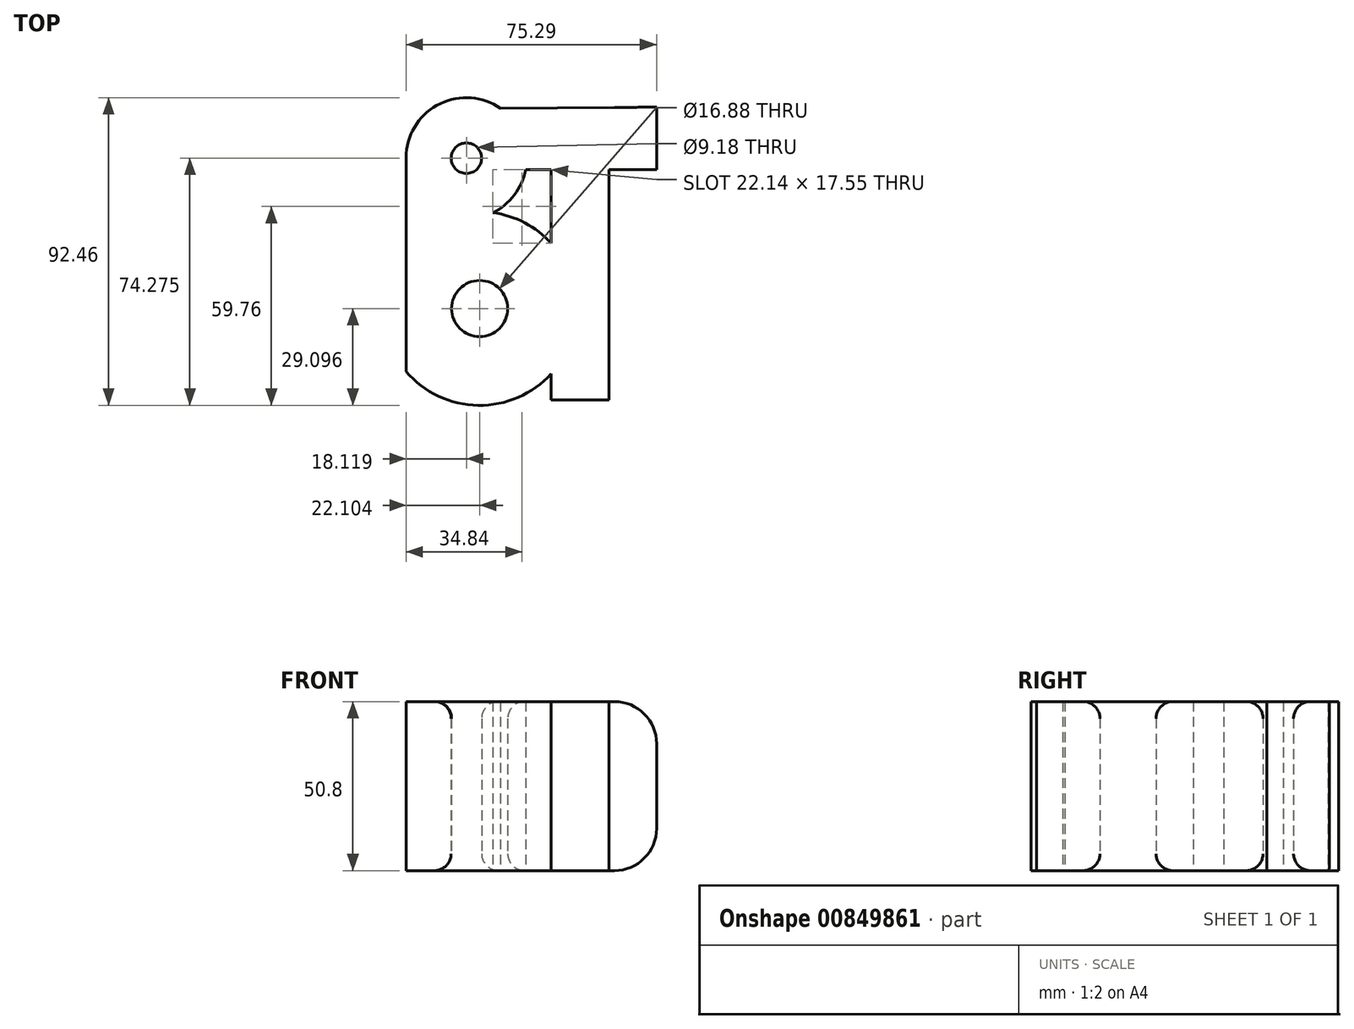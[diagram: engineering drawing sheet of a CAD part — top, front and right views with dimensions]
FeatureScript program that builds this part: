
annotation { "Feature Type Name" : "Feature", "Feature Type Description" : "" }
export const myFeature = defineFeature(function(context is Context, id is Id, definition is map)
    precondition{}
    {
        {
            var Q0;
            Q0=qCreatedBy(makeId("Top.planeOp"),FACE);
            var sketch = newSketch(context, id + "F0", { "sketchPlane" : qUnion([Q0])});
            skLineSegment(sketch, "E0", {"start": v(-40.97, 20.71) * mm, "end": v(-40.97, -44.84) * mm});
            skArc(sketch, "E1", {"start": v(-14.9, 2.9) * mm, "mid": v(-12.6, 34.27) * mm, "end": v(-40.97, 20.71) * mm});
            skArc(sketch, "E2", {"start": v(-40.97, -44.84) * mm, "mid": v(6.67, -39.87) * mm, "end": v(-14.9, 2.9) * mm});
            skLineSegment(sketch, "E3", {"start": v(-12.6, 34.27) * mm, "end": v(34.32, 34.6) * mm});
            skLineSegment(sketch, "E4", {"start": v(34.32, 34.6) * mm, "end": v(34.32, 15.8) * mm});
            skLineSegment(sketch, "E5", {"start": v(34.32, 15.8) * mm, "end": v(20.06, 15.8) * mm});
            skLineSegment(sketch, "E6", {"start": v(20.06, 15.8) * mm, "end": v(20.06, -53.36) * mm});
            skLineSegment(sketch, "E7", {"start": v(20.06, -53.36) * mm, "end": v(2.65, -53.36) * mm});
            skLineSegment(sketch, "E8", {"start": v(2.65, -53.36) * mm, "end": v(2.65, -45.52) * mm});
            skLineSegment(sketch, "E9", {"start": v(2.65, 15.8) * mm, "end": v(-5, 15.8) * mm});
            skPoint(sketch, "E10", {"position": v(-13.33, 25.64) * mm});
            skPoint(sketch, "E11", {"position": v(34.32, 34.6) * mm});
            skLineSegment(sketch, "E12.trimOffspring", {"start": v(2.65, -6.33) * mm, "end": v(2.65, 15.8) * mm});
            skCircle(sketch, "E13", {"center": v(-22.85, 19.26) * mm, "radius": 4.59 * mm});
            skCircle(sketch, "E14", {"center": v(-18.87, -25.92) * mm, "radius": 8.44 * mm});
            skSolve(sketch);
        }
        {
            var Q0;
            Q0 = qSketchRegion(id + "F0", true);
            extrude(context, id + "F1", {"entities" : qUnion([Q0]), "depth" : 50.8 * mm, "offsetDistance" : 25.4 * mm});
        }
        {
            var Q0;
            Q0=makeQuery(id+"F1.opExtrude","CAP_EDGE",EDGE,{"disambiguationData":[OSD([sQuery(id+"F0.wireOp",EDGE,"E4")])],"isStart":false});
            fillet(context, id + "F2", {"entities" : qUnion([Q0]), "radius" : 12.7 * mm, "tangentPropagation" : true, "allowEdgeOverflow" : false});
        }
        {
            var Q0;
            Q0=makeQuery(id+"F1.opExtrude","SWEPT_FACE",FACE,{"disambiguationData":[OSD([sQuery(id+"F0.wireOp",EDGE,"E14")])]});
            var Q1;
            Q1=makeQuery(id+"F1.opExtrude","CAP_EDGE",EDGE,{"disambiguationData":[OSD([sQuery(id+"F0.wireOp",EDGE,"E13")])],"isStart":false});
            fillet(context, id + "F3", {"entities" : qUnion([Q0, Q1]), "radius" : 5.08 * mm, "tangentPropagation" : true, "allowEdgeOverflow" : false});
        }
        {
            var Q0;
            Q0=makeQuery(id+"F1.opExtrude","CAP_EDGE",EDGE,{"disambiguationData":[OSD([sQuery(id+"F0.wireOp",EDGE,"E13")])],"isStart":true});
            fillet(context, id + "F4", {"entities" : qUnion([Q0]), "radius" : 5.08 * mm, "tangentPropagation" : true, "allowEdgeOverflow" : false});
        }
        {
            var Q0;
            Q0=makeQuery(id+"F1.opExtrude","CAP_EDGE",EDGE,{"disambiguationData":[OSD([sQuery(id+"F0.wireOp",EDGE,"E4")])],"isStart":true});
            fillet(context, id + "F5", {"entities" : qUnion([Q0]), "radius" : 12.7 * mm, "tangentPropagation" : true, "allowEdgeOverflow" : false});
        }
    });
